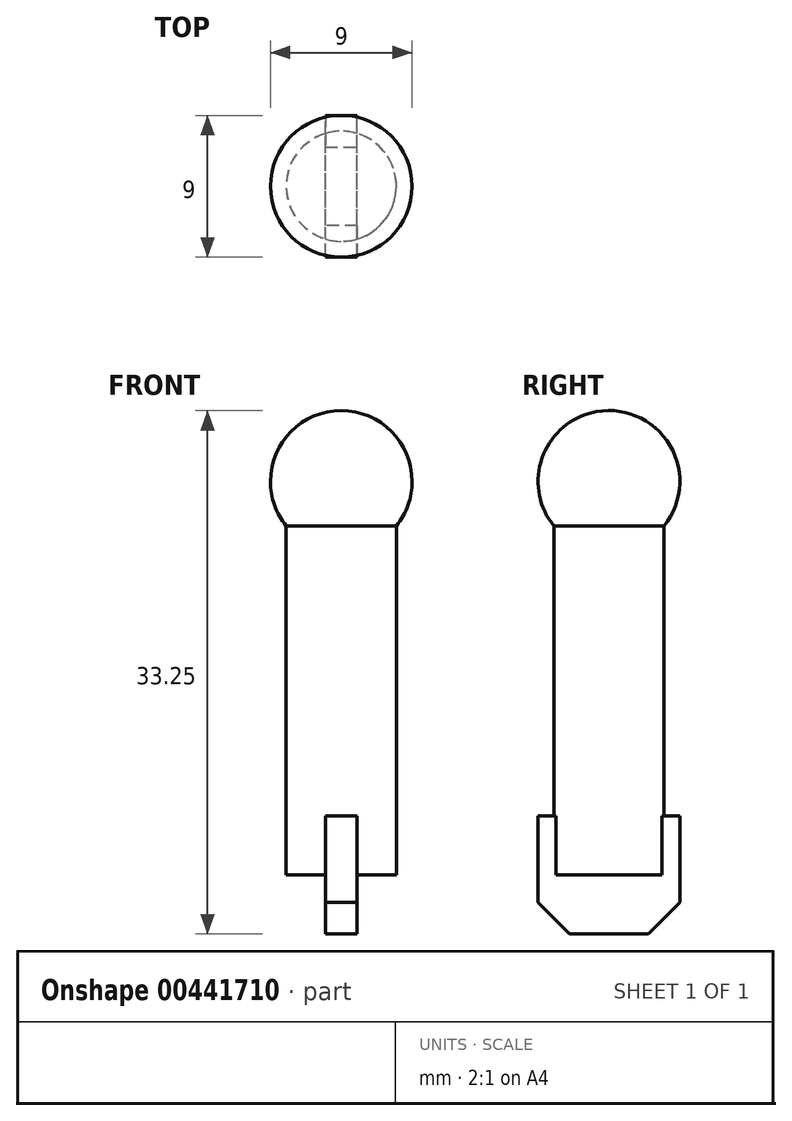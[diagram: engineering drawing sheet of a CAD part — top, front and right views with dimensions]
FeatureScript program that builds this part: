
annotation { "Feature Type Name" : "Feature", "Feature Type Description" : "" }
export const myFeature = defineFeature(function(context is Context, id is Id, definition is map)
    precondition{}
    {
        {
            var Q0;
            Q0=qCreatedBy(makeId("Top.planeOp"),FACE);
            var sketch = newSketch(context, id + "F0", { "sketchPlane" : qUnion([Q0])});
            skCircle(sketch, "E0", {"center": v(0, 0) * mm, "radius": 3.5 * mm});
            skSolve(sketch);
        }
        {
            var Q0;
            Q0 = qSketchRegion(id + "F0", true);
            extrude(context, id + "F1", {"entities" : qUnion([Q0]), "endBound" : BoundingType.SYMMETRIC, "depth" : 25 * mm, "offsetDistance" : 25 * mm});
        }
        {
            var Q0;
            Q0=makeQuery(id+"F1.opExtrude","CAP_FACE",FACE,{"disambiguationData":[OSD([sQuery(id+"F0.wireOp",EDGE,"E0")])],"isStart":true});
            var sketch = newSketch(context, id + "F2", { "sketchPlane" : qUnion([Q0])});
            skLineSegment(sketch, "E1.bottom", {"start": v(-1, 4.5) * mm, "end": v(1, 4.5) * mm});
            skLineSegment(sketch, "E1.top", {"start": v(-1, -4.5) * mm, "end": v(1, -4.5) * mm});
            skLineSegment(sketch, "E1.left", {"start": v(-1, 4.5) * mm, "end": v(-1, -4.5) * mm});
            skLineSegment(sketch, "E1.right", {"start": v(1, 4.5) * mm, "end": v(1, -4.5) * mm});
            skLineSegment(sketch, "E2", {"start": v(0, 7.38) * mm, "end": v(0, -10.47) * mm, "construction": true});
            skLineSegment(sketch, "E3", {"start": v(-8.23, 0) * mm, "end": v(9.66, 0) * mm, "construction": true});
            skSolve(sketch);
        }
        {
            var Q0;
            Q0 = qSketchRegion(id + "F2", true);
            extrude(context, id + "F3", {"entities" : qUnion([Q0]), "operationType" : NewBodyOperationType.ADD, "endBound" : BoundingType.SYMMETRIC, "depth" : 7.5 * mm, "offsetDistance" : 25 * mm});
        }
        {
            var Q0;
            Q0=makeQuery(id+"F1.opExtrude","CAP_FACE",FACE,{"disambiguationData":[OSD([sQuery(id+"F0.wireOp",EDGE,"E0")])],"isStart":false});
            var sketch = newSketch(context, id + "F4", { "sketchPlane" : qUnion([Q0])});
            skLineSegment(sketch, "E4", {"start": v(-3.5, 0) * mm, "end": v(3.5, 0) * mm});
            skSolve(sketch);
        }
        {
            var Q0;
            {var subQ0=sQuery(id+"F4.wireOp",EDGE,"E4");Q0=makeQuery(id+"F4.imprint","IMPRINT",FACE,{"disambiguationData":[TD([[makeQuery(id+"F4.imprint","IMPRINT",EDGE,{"derivedFrom":subQ0}),-1.0]])]});}
            var sketch = newSketch(context, id + "F5", { "sketchPlane" : qUnion([Q0])});
            skArc(sketch, "E5", {"start": v(-4.5, 0) * mm, "mid": v(0, -4.5) * mm, "end": v(4.5, 0) * mm});
            skLineSegment(sketch, "E6", {"start": v(0, 5.6) * mm, "end": v(0, -6.84) * mm, "construction": true});
            skLineSegment(sketch, "E7", {"start": v(-6.79, 0) * mm, "end": v(6.6, 0) * mm, "construction": true});
            skLineSegment(sketch, "E8", {"start": v(-4.5, 0) * mm, "end": v(4.5, 0) * mm});
            skSolve(sketch);
        }
        {
            var Q0;
            Q0 = qSketchRegion(id + "F5", true);
            var Q1;
            Q1=sQuery(id+"F5.wireOp",EDGE,"E7");
            revolve(context, id + "F6", {"operationType" : NewBodyOperationType.ADD, "entities" : qUnion([Q0]), "axis" : qUnion([Q1]), "revolveType" : RevolveType.FULL});
        }
        {
            var Q0;
            Q0=makeQuery(id+"F3.opExtrude","CAP_EDGE",EDGE,{"disambiguationData":[OSD([sQuery(id+"F2.wireOp",EDGE,"E1.bottom")])],"isStart":false});
            var Q1;
            Q1=makeQuery(id+"F3.opExtrude","CAP_EDGE",EDGE,{"disambiguationData":[OSD([sQuery(id+"F2.wireOp",EDGE,"E1.top")])],"isStart":false});
            chamfer(context, id + "F7", {"entities" : qUnion([Q0, Q1]), "width" : 2 * mm, "tangentPropagation" : true});
        }
    });
